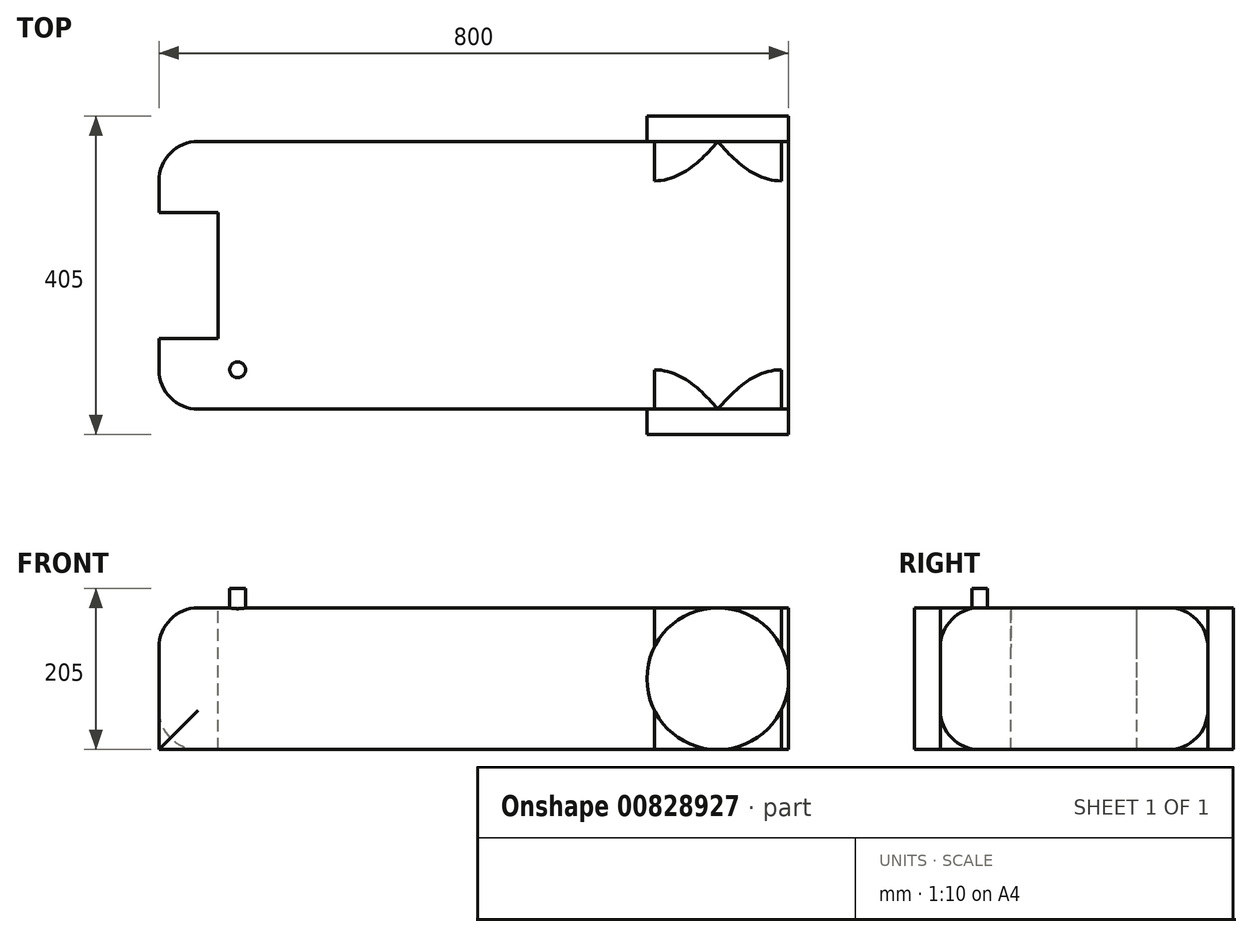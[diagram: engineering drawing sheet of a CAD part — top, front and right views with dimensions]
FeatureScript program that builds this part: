
annotation { "Feature Type Name" : "Feature", "Feature Type Description" : "" }
export const myFeature = defineFeature(function(context is Context, id is Id, definition is map)
    precondition{}
    {
        {
            var Q0;
            Q0=qCreatedBy(makeId("Top.planeOp"),FACE);
            var sketch = newSketch(context, id + "F0", { "sketchPlane" : qUnion([Q0])});
            skLineSegment(sketch, "E0.bottom", {"start": v(400, -170) * mm, "end": v(-400, -170) * mm});
            skLineSegment(sketch, "E0.top", {"start": v(400, 170) * mm, "end": v(-400, 170) * mm});
            skLineSegment(sketch, "E0.left", {"start": v(400, -170) * mm, "end": v(400, 170) * mm});
            skLineSegment(sketch, "E0.right", {"start": v(-400, -170) * mm, "end": v(-400, 170) * mm});
            skPoint(sketch, "E0.middle", {"position": v(0, 0) * mm});
            skSolve(sketch);
        }
        {
            var Q0;
            Q0=makeQuery(id+"F0.imprint","IMPRINT",FACE,{"disambiguationData":[TD([[makeQuery(id+"F0.imprint","IMPRINT",EDGE,{"derivedFrom":sQuery(id+"F0.wireOp",EDGE,"E0.bottom")}),-1.0]])]});
            extrude(context, id + "F1", {"entities" : qUnion([Q0]), "depth" : 180 * mm, "offsetDistance" : 25 * mm});
        }
        {
            var Q0;
            Q0=makeQuery(id+"F1.opExtrude","SWEPT_FACE",FACE,{"disambiguationData":[OSD([sQuery(id+"F0.wireOp",EDGE,"E0.bottom")])]});
            var sketch = newSketch(context, id + "F2", { "sketchPlane" : qUnion([Q0])});
            skLineSegment(sketch, "E1", {"start": v(400, 0) * mm, "end": v(310, 0) * mm});
            skLineSegment(sketch, "E2", {"start": v(310, 0) * mm, "end": v(310, 90) * mm});
            skCircle(sketch, "E3", {"center": v(310, 90) * mm, "radius": 90 * mm});
            skSolve(sketch);
        }
        {
            var Q0;
            {var subQ0=sQuery(id+"F2.wireOp",EDGE,"E3");var subQ1=sQuery(id+"F0.wireOp",EDGE,"E0.bottom");var subQ2=makeQuery(id+"F2.imprint","INTERSECT",VERTEX,{"derivedFrom":[makeQuery(id+"F1.opExtrude","CAP_EDGE",EDGE,{"disambiguationData":[OSD([subQ1])],"isStart":false}),subQ0]});Q0=makeQuery(id+"F2.imprint","IMPRINT",FACE,{"disambiguationData":[TD([[makeQuery(id+"F2.imprint","IMPRINT",EDGE,{"disambiguationData":[TD([[subQ2,1.0]])],"derivedFrom":subQ0}),1.0]])]});}
            extrude(context, id + "F3", {"entities" : qUnion([Q0]), "endBound" : BoundingType.SYMMETRIC, "depth" : 65 * mm, "offsetDistance" : 25 * mm});
        }
        {
            var Q0;
            Q0=makeQuery(id+"F3.opExtrude","SWEPT_BODY",BODY,{"disambiguationData":[OSD([sQuery(id+"F2.wireOp",EDGE,"E3")])]});
            var Q1;
            Q1=qCreatedBy(makeId("Front.planeOp"),FACE);
            mirror(context, id + "F4", {"operationType" : NewBodyOperationType.ADD, "entities" : qUnion([Q0]), "mirrorPlane" : qUnion([Q1])});
        }
        {
            var Q0;
            Q0=makeQuery(id+"F1.opExtrude","CAP_FACE",FACE,{"disambiguationData":[OSD([sQuery(id+"F0.wireOp",EDGE,"E0.bottom"),sQuery(id+"F0.wireOp",EDGE,"E0.top"),sQuery(id+"F0.wireOp",EDGE,"E0.left"),sQuery(id+"F0.wireOp",EDGE,"E0.right")])],"isStart":false});
            var sketch = newSketch(context, id + "F5", { "sketchPlane" : qUnion([Q0])});
            skLineSegment(sketch, "E4", {"start": v(-400, -170) * mm, "end": v(-300, -170) * mm});
            skLineSegment(sketch, "E5", {"start": v(-300, -170) * mm, "end": v(-300, -120) * mm});
            skCircle(sketch, "E6", {"center": v(-300, -120) * mm, "radius": 10 * mm});
            skLineSegment(sketch, "E7", {"start": v(-400, 170) * mm, "end": v(-400, 80) * mm});
            skLineSegment(sketch, "E8", {"start": v(-400, -170) * mm, "end": v(-400, -80) * mm});
            skLineSegment(sketch, "E9", {"start": v(-400, -80) * mm, "end": v(-325, -80) * mm});
            skLineSegment(sketch, "E10", {"start": v(-325, -80) * mm, "end": v(-325, 80) * mm});
            skLineSegment(sketch, "E11", {"start": v(-325, 80) * mm, "end": v(-400, 80) * mm});
            skSolve(sketch);
        }
        {
            var Q0;
            Q0=makeQuery(id+"F5.imprint","IMPRINT",FACE,{"disambiguationData":[TD([[makeQuery(id+"F5.imprint","IMPRINT",EDGE,{"derivedFrom":sQuery(id+"F5.wireOp",EDGE,"E6")}),1.0]])]});
            extrude(context, id + "F6", {"entities" : qUnion([Q0]), "operationType" : NewBodyOperationType.ADD, "depth" : 25 * mm, "offsetDistance" : 25 * mm});
        }
        {
            var Q0;
            {var subQ0=sQuery(id+"F5.wireOp",EDGE,"E9");Q0=makeQuery(id+"F5.imprint","IMPRINT",FACE,{"disambiguationData":[TD([[makeQuery(id+"F5.imprint","IMPRINT",EDGE,{"derivedFrom":subQ0}),1.0]])]});}
            extrude(context, id + "F7", {"entities" : qUnion([Q0]), "operationType" : NewBodyOperationType.REMOVE, "oppositeDirection" : true, "depth" : 180 * mm, "offsetDistance" : 25 * mm});
        }
        {
            var Q0;
            {var subQ0=sQuery(id+"F0.wireOp",EDGE,"E0.right");var subQ1=sQuery(id+"F0.wireOp",EDGE,"E0.top");Q0=makeQuery(id+"F4.boolean.opBoolean","SPLIT",EDGE,{"disambiguationData":[TD([makeQuery(id+"F1.opExtrude","SWEPT_FACE",FACE,{"disambiguationData":[OSD([subQ0])]})])],"derivedFrom":makeQuery(id+"F1.opExtrude","CAP_EDGE",EDGE,{"disambiguationData":[OSD([subQ1])],"isStart":false})});}
            var Q1;
            {var subQ0=sQuery(id+"F0.wireOp",EDGE,"E0.right");var subQ1=sQuery(id+"F0.wireOp",EDGE,"E0.top");Q1=makeQuery(id+"F7.boolean.opBoolean","SPLIT",EDGE,{"disambiguationData":[TD([makeQuery(id+"F1.opExtrude","SWEPT_FACE",FACE,{"disambiguationData":[OSD([subQ1])]})])],"derivedFrom":makeQuery(id+"F1.opExtrude","CAP_EDGE",EDGE,{"disambiguationData":[OSD([subQ0])],"isStart":false})});}
            var Q2;
            Q2=makeQuery(id+"F7.boolean.opBoolean","COPY",EDGE,{"derivedFrom":makeQuery(id+"F7.opExtrude","CAP_EDGE",EDGE,{"disambiguationData":[OSD([sQuery(id+"F5.wireOp",EDGE,"E10")])],"isStart":true})});
            var Q3;
            {var subQ0=sQuery(id+"F0.wireOp",EDGE,"E0.bottom");var subQ1=sQuery(id+"F0.wireOp",EDGE,"E0.right");Q3=makeQuery(id+"F7.boolean.opBoolean","SPLIT",EDGE,{"disambiguationData":[TD([makeQuery(id+"F1.opExtrude","SWEPT_FACE",FACE,{"disambiguationData":[OSD([subQ0])]})])],"derivedFrom":makeQuery(id+"F1.opExtrude","CAP_EDGE",EDGE,{"disambiguationData":[OSD([subQ1])],"isStart":false})});}
            var Q4;
            {var subQ0=sQuery(id+"F0.wireOp",EDGE,"E0.bottom");var subQ1=sQuery(id+"F0.wireOp",EDGE,"E0.right");Q4=makeQuery(id+"F4.boolean.opBoolean","SPLIT",EDGE,{"disambiguationData":[TD([makeQuery(id+"F1.opExtrude","SWEPT_FACE",FACE,{"disambiguationData":[OSD([subQ1])]})])],"derivedFrom":makeQuery(id+"F1.opExtrude","CAP_EDGE",EDGE,{"disambiguationData":[OSD([subQ0])],"isStart":false})});}
            var Q5;
            {var subQ0=sQuery(id+"F0.wireOp",EDGE,"E0.bottom");var subQ1=sQuery(id+"F0.wireOp",EDGE,"E0.right");Q5=makeQuery(id+"F4.boolean.opBoolean","SPLIT",EDGE,{"disambiguationData":[TD([makeQuery(id+"F1.opExtrude","SWEPT_FACE",FACE,{"disambiguationData":[OSD([subQ1])]})])],"derivedFrom":makeQuery(id+"F1.opExtrude","CAP_EDGE",EDGE,{"disambiguationData":[OSD([subQ0])],"isStart":true})});}
            var Q6;
            Q6=makeQuery(id+"F1.opExtrude","SWEPT_EDGE",EDGE,{"disambiguationData":[OSD([sQuery(id+"F0.wireOp",EDGE,"E0.bottom"),sQuery(id+"F0.wireOp",EDGE,"E0.right")])]});
            var Q7;
            Q7=makeQuery(id+"F1.opExtrude","SWEPT_EDGE",EDGE,{"disambiguationData":[OSD([sQuery(id+"F0.wireOp",EDGE,"E0.top"),sQuery(id+"F0.wireOp",EDGE,"E0.right")])]});
            var Q8;
            {var subQ0=sQuery(id+"F0.wireOp",EDGE,"E0.right");var subQ1=sQuery(id+"F0.wireOp",EDGE,"E0.top");Q8=makeQuery(id+"F7.boolean.opBoolean","SPLIT",EDGE,{"disambiguationData":[TD([makeQuery(id+"F1.opExtrude","SWEPT_FACE",FACE,{"disambiguationData":[OSD([subQ1])]})])],"derivedFrom":makeQuery(id+"F1.opExtrude","CAP_EDGE",EDGE,{"disambiguationData":[OSD([subQ0])],"isStart":true})});}
            var Q9;
            Q9=makeQuery(id+"F7.boolean.opBoolean","COPY",EDGE,{"derivedFrom":makeQuery(id+"F7.opExtrude","CAP_EDGE",EDGE,{"disambiguationData":[OSD([sQuery(id+"F5.wireOp",EDGE,"E10")])],"isStart":false})});
            var Q10;
            {var subQ0=sQuery(id+"F0.wireOp",EDGE,"E0.right");var subQ1=sQuery(id+"F0.wireOp",EDGE,"E0.top");Q10=makeQuery(id+"F4.boolean.opBoolean","SPLIT",EDGE,{"disambiguationData":[TD([makeQuery(id+"F1.opExtrude","SWEPT_FACE",FACE,{"disambiguationData":[OSD([subQ0])]})])],"derivedFrom":makeQuery(id+"F1.opExtrude","CAP_EDGE",EDGE,{"disambiguationData":[OSD([subQ1])],"isStart":true})});}
            fillet(context, id + "F8", {"entities" : qUnion([Q0, Q1, Q2, Q3, Q4, Q5, Q6, Q7, Q8, Q9, Q10]), "radius" : 50 * mm, "tangentPropagation" : true, "allowEdgeOverflow" : false});
        }
    });
